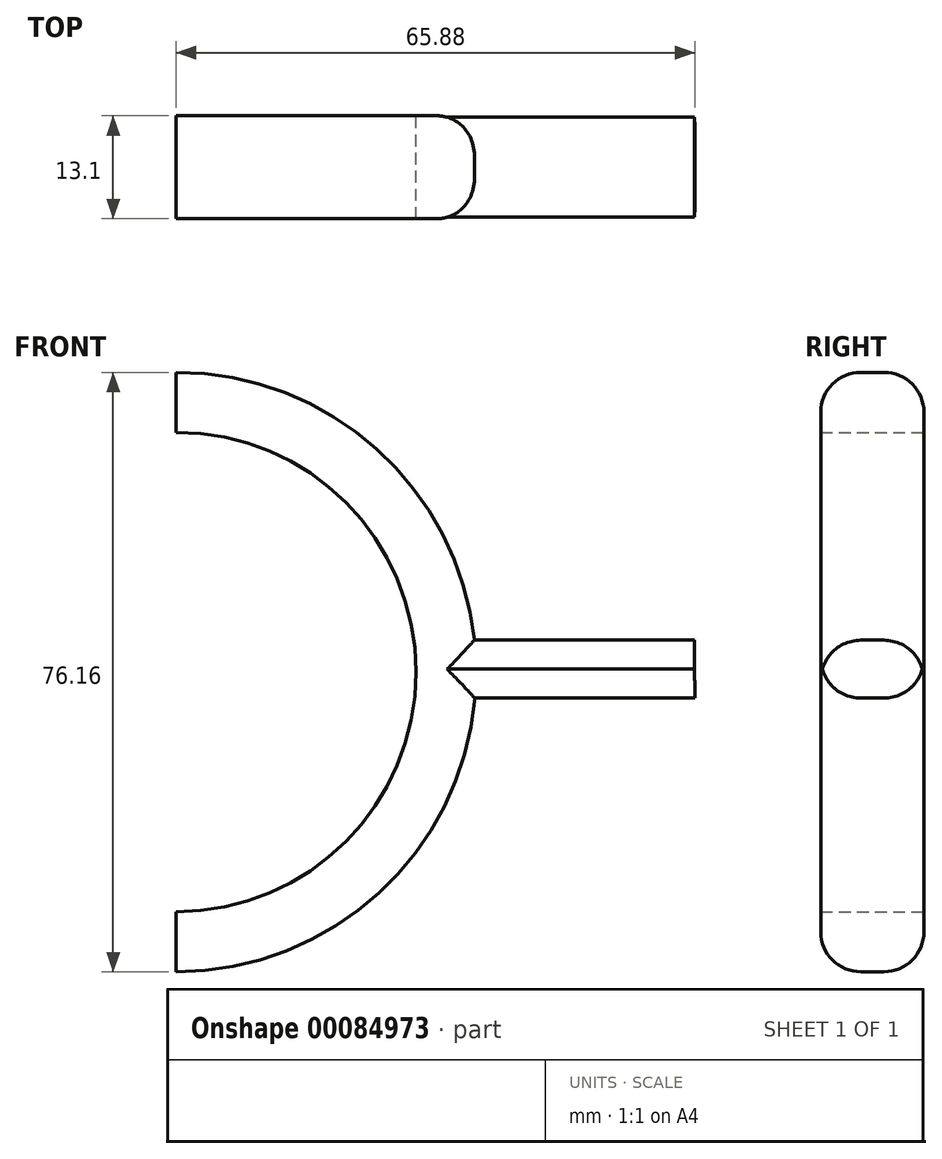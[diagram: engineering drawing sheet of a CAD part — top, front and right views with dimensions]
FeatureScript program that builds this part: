
annotation { "Feature Type Name" : "Feature", "Feature Type Description" : "" }
export const myFeature = defineFeature(function(context is Context, id is Id, definition is map)
    precondition{}
    {
        {
            var Q0;
            Q0=qCreatedBy(makeId("Front.planeOp"),FACE);
            var sketch = newSketch(context, id + "F0", { "sketchPlane" : qUnion([Q0])});
            skArc(sketch, "E0", {"start": v(0, -38.08) * mm, "mid": v(38.08, 0) * mm, "end": v(0, 38.08) * mm});
            skLineSegment(sketch, "E1", {"start": v(0, 38.08) * mm, "end": v(0, 30.46) * mm});
            skLineSegment(sketch, "E2", {"start": v(0, -38.08) * mm, "end": v(0, -30.46) * mm});
            skArc(sketch, "E3", {"start": v(0, -30.46) * mm, "mid": v(30.46, 0) * mm, "end": v(0, 30.46) * mm});
            skLineSegment(sketch, "E4", {"start": v(37.94, -3.31) * mm, "end": v(65.88, -3.31) * mm});
            skLineSegment(sketch, "E5", {"start": v(37.86, 4.05) * mm, "end": v(65.8, 4.05) * mm});
            skPoint(sketch, "E6.end.orphan", {"position": v(65.88, 2.27) * mm});
            skPoint(sketch, "E6.start.orphan", {"position": v(38.08, 0) * mm});
            skLineSegment(sketch, "E7", {"start": v(65.8, 4.05) * mm, "end": v(65.88, -3.31) * mm});
            skSolve(sketch);
        }
        {
            var Q0;
            Q0=qCreatedBy(makeId("Right.planeOp"),FACE);
            var sketch = newSketch(context, id + "F1", { "sketchPlane" : qUnion([Q0])});
            skLineSegment(sketch, "E8", {"start": v(0, 0) * mm, "end": v(13.1, 0) * mm});
            skCircle(sketch, "E9", {"center": v(0, 0) * mm, "radius": 8.1 * mm});
            skSolve(sketch);
        }
        {
            var Q0;
            {var subQ0=sQuery(id+"F0.wireOp",EDGE,"E4");Q0=makeQuery(id+"F0.imprint","IMPRINT",FACE,{"disambiguationData":[TD([[makeQuery(id+"F0.imprint","IMPRINT",EDGE,{"derivedFrom":subQ0}),1.0]])]});}
            var Q1;
            {var subQ0=sQuery(id+"F0.wireOp",EDGE,"E1");Q1=makeQuery(id+"F0.imprint","IMPRINT",FACE,{"disambiguationData":[TD([[makeQuery(id+"F0.imprint","IMPRINT",EDGE,{"derivedFrom":subQ0}),1.0]])]});}
            var Q2;
            Q2=sQuery(id+"F0.wireOp",EDGE,"E0");
            var Q3;
            Q3=sQuery(id+"F1.wireOp",EDGE,"E8");
            sweep(context, id + "F2", {"profiles" : qUnion([Q0, Q1]), "surfaceProfiles" : qUnion([Q2]), "path" : qUnion([Q3])});
        }
        {
            var Q0;
            {var subQ0=sQuery(id+"F1.wireOp",VERTEX,"E8.start");var subQ1=sQuery(id+"F0.wireOp",EDGE,"E0");Q0=makeQuery(id+"F2.opSweep","CAP_EDGE",EDGE,{"disambiguationData":[OSD([subQ1,subQ0]),TDD([makeQuery(id+"F0.imprint","IMPRINT",EDGE,{"disambiguationData":[TD([[makeQuery(id+"F0.imprint","INTERSECT",VERTEX,{"derivedFrom":[subQ1,sQuery(id+"F0.wireOp",EDGE,"E1")]}),1.0]])],"derivedFrom":subQ1}),subQ0])],"isStart":true});}
            var Q1;
            {var subQ0=sQuery(id+"F1.wireOp",VERTEX,"E8.start");var subQ1=sQuery(id+"F0.wireOp",EDGE,"E0");Q1=makeQuery(id+"F2.opSweep","CAP_EDGE",EDGE,{"disambiguationData":[OSD([subQ1,subQ0]),TDD([makeQuery(id+"F0.imprint","IMPRINT",EDGE,{"disambiguationData":[TD([[makeQuery(id+"F0.imprint","INTERSECT",VERTEX,{"derivedFrom":[subQ1,sQuery(id+"F0.wireOp",EDGE,"E2")]}),-1.0]])],"derivedFrom":subQ1}),subQ0])],"isStart":true});}
            var Q2;
            Q2=makeQuery(id+"F2.opSweep","CAP_EDGE",EDGE,{"disambiguationData":[OSD([sQuery(id+"F0.wireOp",EDGE,"E5"),sQuery(id+"F1.wireOp",VERTEX,"E8.start")])],"isStart":true});
            var Q3;
            {var subQ0=sQuery(id+"F1.wireOp",VERTEX,"E8.end");var subQ1=sQuery(id+"F0.wireOp",EDGE,"E0");Q3=makeQuery(id+"F2.opSweep","CAP_EDGE",EDGE,{"disambiguationData":[OSD([subQ1,subQ0]),TDD([makeQuery(id+"F0.imprint","IMPRINT",EDGE,{"disambiguationData":[TD([[makeQuery(id+"F0.imprint","INTERSECT",VERTEX,{"derivedFrom":[subQ1,sQuery(id+"F0.wireOp",EDGE,"E2")]}),-1.0]])],"derivedFrom":subQ1}),subQ0])],"isStart":false});}
            var Q4;
            {var subQ0=sQuery(id+"F1.wireOp",VERTEX,"E8.end");var subQ1=sQuery(id+"F0.wireOp",EDGE,"E0");Q4=makeQuery(id+"F2.opSweep","CAP_EDGE",EDGE,{"disambiguationData":[OSD([subQ1,subQ0]),TDD([makeQuery(id+"F0.imprint","IMPRINT",EDGE,{"disambiguationData":[TD([[makeQuery(id+"F0.imprint","INTERSECT",VERTEX,{"derivedFrom":[subQ1,sQuery(id+"F0.wireOp",EDGE,"E1")]}),1.0]])],"derivedFrom":subQ1}),subQ0])],"isStart":false});}
            var Q5;
            Q5=makeQuery(id+"F2.opSweep","CAP_EDGE",EDGE,{"disambiguationData":[OSD([sQuery(id+"F0.wireOp",EDGE,"E5"),sQuery(id+"F1.wireOp",VERTEX,"E8.end")])],"isStart":false});
            var Q6;
            Q6=makeQuery(id+"F2.opSweep","CAP_EDGE",EDGE,{"disambiguationData":[OSD([sQuery(id+"F0.wireOp",EDGE,"E4"),sQuery(id+"F1.wireOp",VERTEX,"E8.end")])],"isStart":false});
            var Q7;
            Q7=makeQuery(id+"F2.opSweep","CAP_EDGE",EDGE,{"disambiguationData":[OSD([sQuery(id+"F0.wireOp",EDGE,"E4"),sQuery(id+"F1.wireOp",VERTEX,"E8.start")])],"isStart":true});
            fillet(context, id + "F3", {"entities" : qUnion([Q0, Q1, Q2, Q3, Q4, Q5, Q6, Q7]), "radius" : 5.08 * mm, "tangentPropagation" : true, "allowEdgeOverflow" : false});
        }
    });
